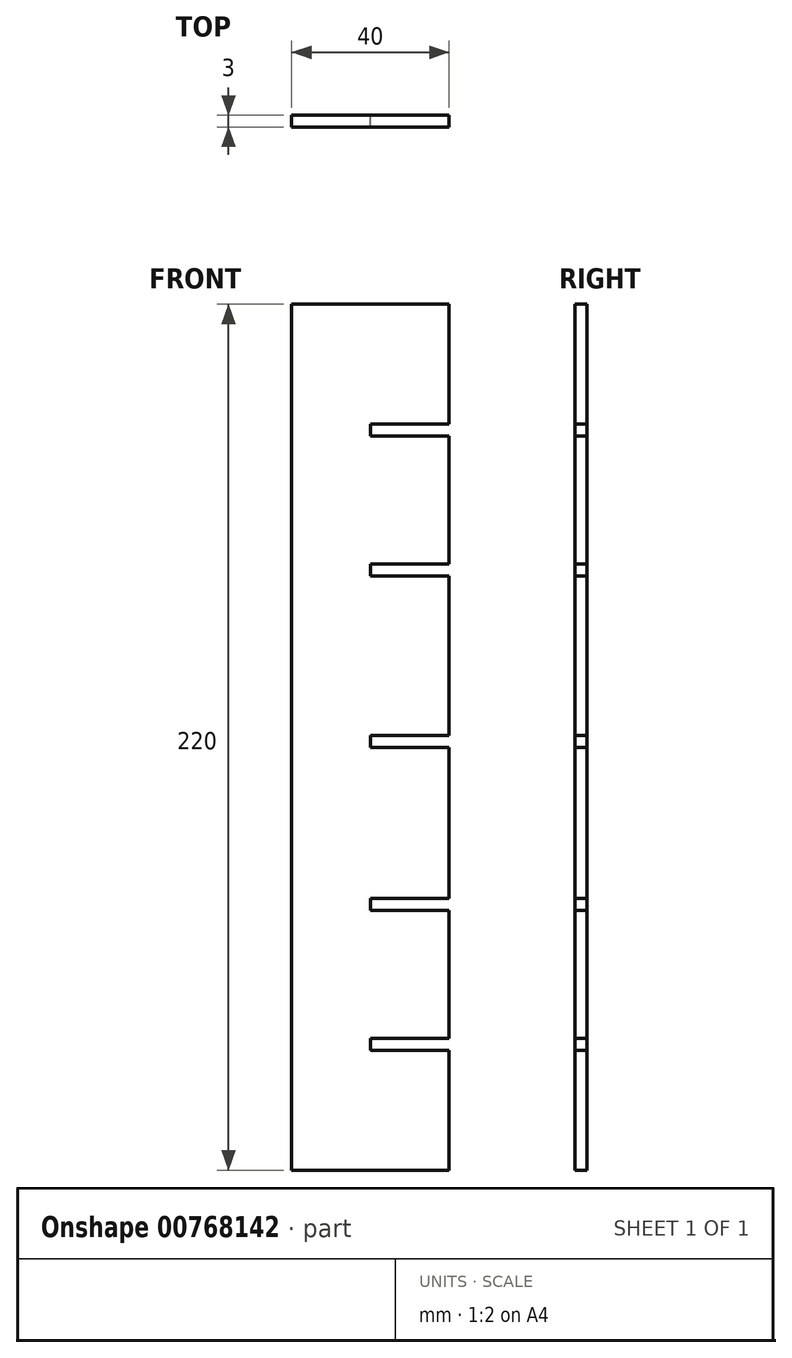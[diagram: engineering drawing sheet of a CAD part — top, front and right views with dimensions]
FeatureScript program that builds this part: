
annotation { "Feature Type Name" : "Feature", "Feature Type Description" : "" }
export const myFeature = defineFeature(function(context is Context, id is Id, definition is map)
    precondition{}
    {
        {
            var Q0;
            Q0=qCreatedBy(makeId("Front.planeOp"),FACE);
            var sketch = newSketch(context, id + "F0", { "sketchPlane" : qUnion([Q0])});
            skLineSegment(sketch, "E0.bottom", {"start": v(-20, 110) * mm, "end": v(20, 110) * mm});
            skLineSegment(sketch, "E0.top", {"start": v(-20, -110) * mm, "end": v(20, -110) * mm});
            skLineSegment(sketch, "E0.left", {"start": v(-20, 110) * mm, "end": v(-20, -110) * mm});
            skLineSegment(sketch, "E0.right", {"start": v(20, 110) * mm, "end": v(20, -110) * mm});
            skPoint(sketch, "E0.middle", {"position": v(0, 0) * mm});
            skLineSegment(sketch, "E1.bottom", {"start": v(20, 76.57) * mm, "end": v(0, 76.57) * mm});
            skLineSegment(sketch, "E1.top", {"start": v(20, 79.58) * mm, "end": v(0, 79.58) * mm});
            skLineSegment(sketch, "E1.left", {"start": v(20, 76.57) * mm, "end": v(20, 79.58) * mm});
            skLineSegment(sketch, "E1.right", {"start": v(0, 76.57) * mm, "end": v(0, 79.58) * mm});
            skLineSegment(sketch, "E2.MirrorCS", {"start": v(0, -76.57) * mm, "end": v(0, -79.58) * mm});
            skLineSegment(sketch, "E3.MirrorCS", {"start": v(20, -76.57) * mm, "end": v(20, -79.58) * mm});
            skLineSegment(sketch, "E4.MirrorCS", {"start": v(20, -79.58) * mm, "end": v(0, -79.58) * mm});
            skLineSegment(sketch, "E5.MirrorCS", {"start": v(20, -76.57) * mm, "end": v(0, -76.57) * mm});
            skLineSegment(sketch, "E6.bottom", {"start": v(20, 44.02) * mm, "end": v(0, 44.02) * mm});
            skLineSegment(sketch, "E6.top", {"start": v(20, 41) * mm, "end": v(0, 41) * mm});
            skLineSegment(sketch, "E6.left", {"start": v(20, 44.02) * mm, "end": v(20, 41) * mm});
            skLineSegment(sketch, "E6.right", {"start": v(0, 44.02) * mm, "end": v(0, 41) * mm});
            skLineSegment(sketch, "E7.MirrorCS", {"start": v(20, -44.02) * mm, "end": v(20, -41) * mm});
            skLineSegment(sketch, "E8.MirrorCS", {"start": v(0, -44.02) * mm, "end": v(0, -41) * mm});
            skLineSegment(sketch, "E9.MirrorCS", {"start": v(20, -41) * mm, "end": v(0, -41) * mm});
            skLineSegment(sketch, "E10.MirrorCS", {"start": v(20, -44.02) * mm, "end": v(0, -44.02) * mm});
            skLineSegment(sketch, "E11.bottom", {"start": v(20, 0.4) * mm, "end": v(0, 0.4) * mm});
            skLineSegment(sketch, "E11.top", {"start": v(20, -2.6) * mm, "end": v(0, -2.6) * mm});
            skLineSegment(sketch, "E11.left", {"start": v(20, 0.4) * mm, "end": v(20, -2.6) * mm});
            skLineSegment(sketch, "E11.right", {"start": v(0, 0.4) * mm, "end": v(0, -2.6) * mm});
            skSolve(sketch);
        }
        {
            var Q0;
            {var subQ6=sQuery(id+"F0.wireOp",EDGE,"E0.bottom");Q0=makeQuery(id+"F0.imprint","IMPRINT",FACE,{"disambiguationData":[TD([[makeQuery(id+"F0.imprint","IMPRINT",EDGE,{"derivedFrom":subQ6}),-1.0]])]});}
            extrude(context, id + "F1", {"entities" : qUnion([Q0]), "depth" : 3 * mm, "offsetDistance" : 25.4 * mm});
        }
    });
